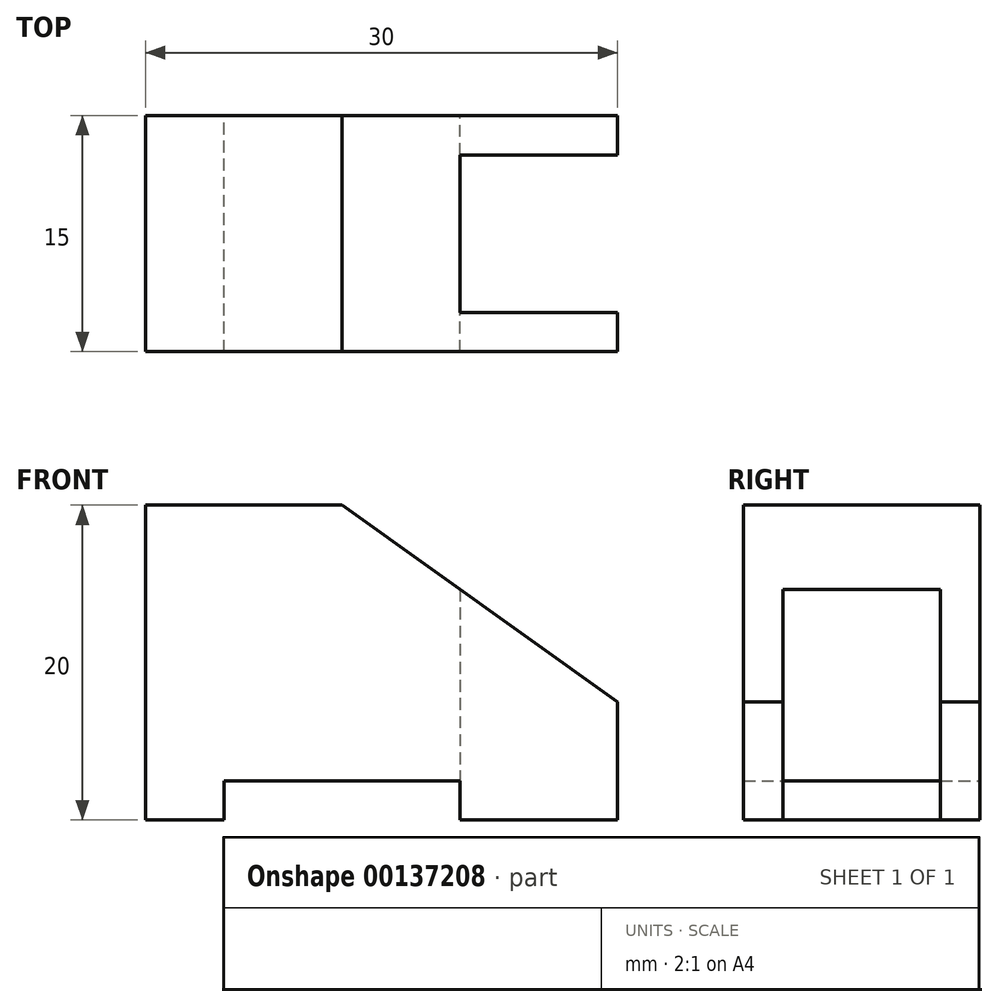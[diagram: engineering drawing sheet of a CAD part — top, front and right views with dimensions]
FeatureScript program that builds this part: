
annotation { "Feature Type Name" : "Feature", "Feature Type Description" : "" }
export const myFeature = defineFeature(function(context is Context, id is Id, definition is map)
    precondition{}
    {
        {
            var Q0;
            Q0=qCreatedBy(makeId("Front.planeOp"),FACE);
            var sketch = newSketch(context, id + "F0", { "sketchPlane" : qUnion([Q0])});
            skLineSegment(sketch, "E0", {"start": v(0, 0) * mm, "end": v(5, 0) * mm});
            skLineSegment(sketch, "E1", {"start": v(5, 0) * mm, "end": v(5, 2.5) * mm});
            skLineSegment(sketch, "E2", {"start": v(5, 2.5) * mm, "end": v(20, 2.5) * mm});
            skLineSegment(sketch, "E3", {"start": v(20, 2.5) * mm, "end": v(20, 0) * mm});
            skLineSegment(sketch, "E4", {"start": v(20, 0) * mm, "end": v(30, 0) * mm});
            skLineSegment(sketch, "E5", {"start": v(30, 0) * mm, "end": v(30, 7.5) * mm});
            skLineSegment(sketch, "E6", {"start": v(30, 7.5) * mm, "end": v(12.5, 20) * mm});
            skLineSegment(sketch, "E7", {"start": v(12.5, 20) * mm, "end": v(0, 20) * mm});
            skLineSegment(sketch, "E8", {"start": v(0, 20) * mm, "end": v(0, 0) * mm});
            skSolve(sketch);
        }
        {
            var Q0;
            Q0 = qSketchRegion(id + "F0", true);
            extrude(context, id + "F1", {"entities" : qUnion([Q0]), "depth" : 15 * mm});
        }
        {
            var Q0;
            Q0=makeQuery(id+"F1.opExtrude","SWEPT_FACE",FACE,{"disambiguationData":[OSD([sQuery(id+"F0.wireOp",EDGE,"E4")])]});
            var sketch = newSketch(context, id + "F2", { "sketchPlane" : qUnion([Q0])});
            skLineSegment(sketch, "E9", {"start": v(30, 12.5) * mm, "end": v(20, 12.5) * mm});
            skLineSegment(sketch, "E10", {"start": v(20, 12.5) * mm, "end": v(20, 2.5) * mm});
            skLineSegment(sketch, "E11", {"start": v(20, 2.5) * mm, "end": v(30, 2.5) * mm});
            skLineSegment(sketch, "E12", {"start": v(30, 2.5) * mm, "end": v(30, 12.5) * mm});
            skSolve(sketch);
        }
        {
            var Q0;
            Q0 = qSketchRegion(id + "F2", true);
            extrude(context, id + "F3", {"entities" : qUnion([Q0]), "operationType" : NewBodyOperationType.REMOVE, "oppositeDirection" : true, "depth" : 25 * mm});
        }
    });
